# Revit family: СВЕТОДИОДНАЯ ПАНЕЛЬ
name_source: partatom
category: Осветительные приборы
revit_build: Autodesk Revit 2016 (Build: 20151007_0715(x64)
units: mm (PartAtom-declared; Revit-internal decimal feet)

## family parameters
Источник света = Да
Общий = Нет
Основа = Грань
При загрузке вырезать с полостями = Да
Размер круглого соединителя = Использовать диаметр
Тип детали = Нормальный
Точка расчета площади = Нет

## types (2) — shared parameters
ADSK_Единица измерения = Шт.
ADSK_Завод-изготовитель = ГК «Вартон»
ADSK_Количество фаз = 1
ADSK_Количество фаз числовое = 1
ADSK_Коэффициент мощности = 0.95
ADSK_Масса = 0.145
ADSK_Напряжение = 220 В
ADSK_Номинальная мощность = 0 кВт
ADSK_Полная мощность = 0 кВ·А
ADSK_Размер_Высота = 10 мм
ADSK_Размер_Длина = 595 мм
ADSK_Размер_Ширина = 595 мм
ADSK_Ток = 0 А
ADSK_Энергоэффективность = 0 лм/Вт
IP Class = IP20
URL = http://varton.ru
Блок аварийного питания = Нет
Видимая форма излучения при визуализации = Нет
Группа модели = Светильники
Изготовитель = ГК «Вартон»
Излучение по длине прямоугольника = 588 мм
Излучение по ширине прямоугольника = 588 мм
Класс Защиты = II
Класс пожароопасности = нет
Климатическая зона = УХЛ4
Корпус = Корпус белый металл
Область использования = Рекомендован для освещения административных помещений
Плафон = Плафон самосвечение
Полная установленная мощность = 0 кВ·А
Разработчик = ООО ПРОРУБИМ
Разработчик (телефон) = +7 (495) 649-85-43
Разработчик модели (URL) = http://prorubim.com
Светофильтр = 16777215
Смещение цветовой температуры при затухании лампы = <Нет>
Тип ИС = LED
Тип рассеивателя = Рассеиватель Светодиодная панель : V2-A0-OP00-03.2.0007.15 Опал
УОИС = УОИС : Светильник светодиодный
Угол наклона = -90.00°
Файл фотометрической сетки = LD936511243.ies
zero-valued in all types: Отметка по умолчанию

## per-type parameters (varying)
| type | ADSK_Код изделия | ADSK_Наименование | Описание | Тип продукции |
| LD936511243_Опал | LD936511243 | Светодиодный светильник ВАРТОН панель 595*595*10 мм IP20 34Вт 4000K | Светодиодный светильник ВАРТОН панель 595*595*10 мм IP20 34Вт 4000K | Светодиодный светильник ВАРТОН панель 595*595*10 мм IP20 34Вт 4000K |
| LD936511343_Опал | LD936511343 | Светодиодный светильник ВАРТОН панель 595*595*10 мм IP20 34Вт 6500K | Светодиодный светильник ВАРТОН панель 595*595*10 мм IP20 34Вт 6500K | Светодиодный светильник ВАРТОН панель 595*595*10 мм IP20 34Вт 6500K |

## geometry (parser evidence)
native form markers: Blend x2
no freeform markers — native parametric forms only
